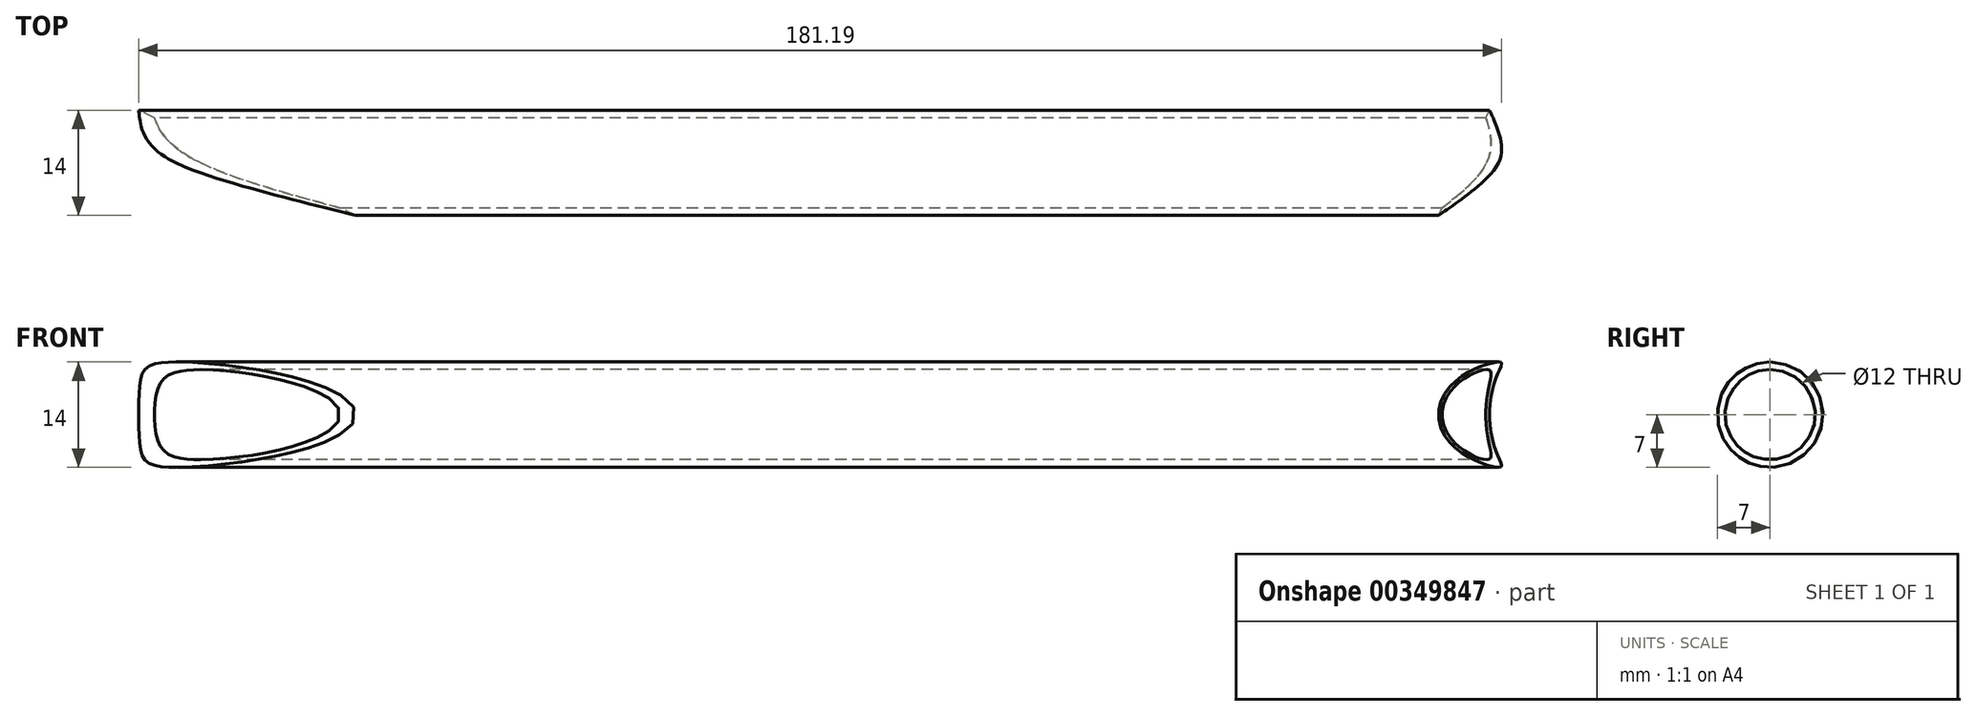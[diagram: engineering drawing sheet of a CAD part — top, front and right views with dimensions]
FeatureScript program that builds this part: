
annotation { "Feature Type Name" : "Feature", "Feature Type Description" : "" }
export const myFeature = defineFeature(function(context is Context, id is Id, definition is map)
    precondition{}
    {
        {
            var Q0;
            Q0=qCreatedBy(makeId("Right.planeOp"),FACE);
            var sketch = newSketch(context, id + "F0", { "sketchPlane" : qUnion([Q0])});
            skCircle(sketch, "E0", {"center": v(0, 0) * mm, "radius": 7 * mm});
            skCircle(sketch, "E1", {"center": v(0, 0) * mm, "radius": 6 * mm});
            skSolve(sketch);
        }
        {
            var Q0;
            Q0 = qSketchRegion(id + "F0", true);
            extrude(context, id + "F1", {"entities" : qUnion([Q0]), "depth" : 188.96 * mm});
        }
        {
            var Q0;
            Q0=qCreatedBy(makeId("Right.planeOp"),FACE);
            var sketch = newSketch(context, id + "F2", { "sketchPlane" : qUnion([Q0])});
            skLineSegment(sketch, "E2", {"start": v(0, 75.19) * mm, "end": v(0, -75.52) * mm, "construction": true});
            skSolve(sketch);
        }
        {
            var Q0;
            Q0=sQuery(id+"F2.wireOp",EDGE,"E2");
            var Q1;
            Q1 = qBodyType(qCreatedBy(id + "F4" ,EDGE), BodyType.WIRE);
            cPlane(context, id + "F3", {"entities" : qUnion([Q0, Q1]), "cplaneType" : CPlaneType.LINE_ANGLE, "offset" : 25 * mm, "angle" : 25.89 * degree, "width" : 150 * mm, "height" : 150 * mm});
        }
        {
            var Q0;
            Q0=qCreatedBy(id+"F3.planeOp",FACE);
            var sketch = newSketch(context, id + "F4", { "sketchPlane" : qUnion([Q0])});
            skCircle(sketch, "E3", {"center": v(0, 0) * mm, "radius": 8 * mm});
            skSolve(sketch);
        }
        {
            var Q0;
            Q0 = qSketchRegion(id + "F4", true);
            extrude(context, id + "F5", {"entities" : qUnion([Q0]), "operationType" : NewBodyOperationType.REMOVE, "endBound" : BoundingType.SYMMETRIC, "oppositeDirection" : true, "depth" : 70 * mm});
        }
        {
            var Q0;
            Q0=makeQuery(id+"F1.opExtrude","CAP_FACE",FACE,{"disambiguationData":[OSD([sQuery(id+"F0.wireOp",EDGE,"E0"),sQuery(id+"F0.wireOp",EDGE,"E1")])],"isStart":false});
            var sketch = newSketch(context, id + "F6", { "sketchPlane" : qUnion([Q0])});
            skLineSegment(sketch, "E4", {"start": v(0, -7) * mm, "end": v(0, 7) * mm, "construction": true});
            skSolve(sketch);
        }
        {
            var Q0;
            Q0=sQuery(id+"F6.wireOp",EDGE,"E4");
            cPlane(context, id + "F7", {"entities" : qUnion([Q0]), "cplaneType" : CPlaneType.LINE_ANGLE, "offset" : 25 * mm, "angle" : 64.11 * degree, "width" : 150 * mm, "height" : 150 * mm});
        }
        {
            var Q0;
            Q0=qCreatedBy(id+"F7.planeOp",FACE);
            var sketch = newSketch(context, id + "F8", { "sketchPlane" : qUnion([Q0])});
            skCircle(sketch, "E5", {"center": v(-170, 0) * mm, "radius": 8 * mm});
            skLineSegment(sketch, "E6", {"start": v(-174.76, 5.26) * mm, "end": v(-176, 6.09) * mm});
            skEllipse(sketch, "E7.0", {"center": v(-170, 0) * mm, "majorRadius": 7 * mm, "minorRadius": 3.06 * mm, "majorAxis": v(0, 1), "construction": true});
            skLineSegment(sketch, "E8", {"start": v(-170, 7) * mm, "end": v(-170, -7) * mm, "construction": true});
            skLineSegment(sketch, "E9", {"start": v(-170, 0) * mm, "end": v(-174.34, 0) * mm, "construction": true});
            skSolve(sketch);
        }
        {
            var Q0;
            Q0 = qSketchRegion(id + "F8", true);
            extrude(context, id + "F9", {"entities" : qUnion([Q0]), "operationType" : NewBodyOperationType.REMOVE, "endBound" : BoundingType.SYMMETRIC, "oppositeDirection" : true, "depth" : 30 * mm});
        }
    });
